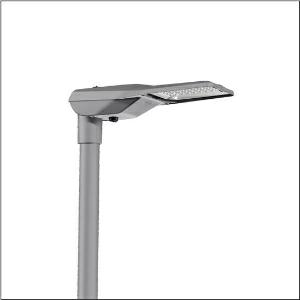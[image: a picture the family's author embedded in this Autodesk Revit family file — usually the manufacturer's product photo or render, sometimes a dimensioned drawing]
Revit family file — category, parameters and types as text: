
# Revit family: streetlight_sl_21_iq_mini___st0_5a_5xe2b31y08hb_0ff0
name_source: partatom
category: Lighting Fixtures
units: mm (PartAtom-declared; Revit-internal decimal feet)

## family parameters
Cut with Voids When Loaded = No
Host = Face
Light Source = No
Part Type = Normal
Room Calculation Point = No
Round Connector Dimension = Use Diameter
Shared = No

## types (1)
- --- (1 x LED, 9750 lm, 71 W, 3000K)
    Apparent Load = 71 VA
    CIE Flux Codes = 41 75 97 100 100
    Color Rendering = 70
    Color Temperature = 3000K
    Default Elevation = 1800 mm
    Description = Streetlight SL 21 iQ mini, mast luminaire, primary light control with lens, of PMMA, primary optical cover: cover, of toughened safety glass, transparent, light distribution: ST0.5a, light emission: direct distribution, primary light characteristic: asymmetric, installation type: post-top, side-entry, LED, High Power LED, rated luminous flux: 9.750lm, luminous efficacy: 137lm/W, light colour: 730, colour temperature: 3000K, control gear: iQ-Street Remote, D4i with power reduction, control: pre-setting: logarithmic dimming characteristic, Street-Remote, Auto-Match, Temp-Guard, Lumen-Switch, Night-Set, Smart-Wire, Light-Fading, Desk-Remote (wireless, voltage-free reading and setting of iQ features in the workshop via application-optimized NFC function/RFID function), optimised constant luminous flux control (CLO 2.0), mains connection: 220..240V, AC, 50/60Hz, start of lifetime: 71W, end of service life: 75W, reduction: 30W, luminaire housing, of diecast aluminium, powder-coated, SITECO metallic grey (DB 702S), corrosivity category C5 high according to DIN EN ISO 12944, please order mast flange separately, inclination adjustable: 0°, 5°, 10°, 15°, sealing non-destructively replaceable, multi-level sealing system, length: 628mm, width: 235mm, height: 110mm, mast flange for spigot size: 42mm (side-entry): 5XC10008XM4, 60/48mm (side-entry/post-top): 5XC10108XM2, 76/60mm (side-entry/post-top): 5XC10108XM1, mounting height: 4..8m, Smart Interface below and above, protection rating (complete): IP66, insulation class (complete): insulation class II (safety insulation), certification: CE, ENEC, ENEC+, VDE, impact resistance: IK10, permissible operating ambient temperature for outdoor applications: -40..+50°C, standard-compliant lighting for roads and squares, packaging unit: 1 piece

Light Distribution: ST0.5a
    Height = 110 mm
    Lamp = 1 x LED
    Lamp Light Flux = 9750 lm
    Lamp Power = 71 W
    Lamp count = 1
    Length = 625 mm
    Luminous efficacy = 137 lm/W
    Manufacturer = Siteco
    ModVariant = No
    Model = 5XE2B31Y08HB
    Mounting Place = Pole
    Mounting Type = Pole top
    Number of Poles = 1
    OnlyDefault = Yes
    Power Factor = 1
    Product Name = Streetlight SL 21 iQ mini | ST0.5a
    Product group = mast luminaire | pylon top
    ProductGroupID = 6100
    Protection Class = Protection class II
    Protection Degree = IP 66
    RLX_Detail_Level = 1
    RLX_Emergency_Light_Flux = 0 lm
    RLX_Emergency_Type = 0
    RLX_Emergency_Type_DB = No
    RlxData = <blob elided: 103665 chars, md5=c3e0a024>
    Socket = socket
    Standby Power = 0 W
    System Light Flux = 9750 lm
    System Power = 71 W
    Type Comments = factory setting: luminous flux: 100 % | dim-lin: 254 | 716 mA
    Type Image = l_1003514.jpg
    URL = http://relux.com
    VarID = @adj_117783
    Voltage = 0 V
    Weight = 0.00 kg
    Width = 234 mm

## geometry (parser evidence)
native form markers: Blend x4, Sweep x10
no freeform markers — native parametric forms only
